# Revit family: Primo S
name_source: partatom
category: Мебель
revit_build: Autodesk Revit 2017 (Build: 20160225_1515(x64)
units: mm (PartAtom-declared; Revit-internal decimal feet)

## family parameters
Всегда вертикально = Да
На основе рабочей плоскости = Нет
Общий = Нет
При загрузке вырезать с полостями = Нет
Точка расчета площади = Нет

## types (6) — shared parameters
Legs Material = Aluminum
Изготовитель = Skandiform AB
Ключевая пометка = XBF.2
Комментарии к типоразмеру = Created by Astacus AB

## per-type parameters (varying)
| type | 092 | 093 | URL | legs type | seat type | Группа модели |
| S-032 | Нет | Нет | http://file-system.ru | Legs 32,33,92&93 | S Seat : S seat | S-032 |
| S-033 | Нет | Нет | http://www.skandiform.com | Legs 32,33,92&93 | H Seat | S-033 |
| S-092 | Да | Нет | http://www.skandiform.com | Legs 32,33,92&93 | S Seat : S seat | S-092 |
| S-082 | Да | Нет | http://www.skandiform.com | Legs 83 | S Seat : S seat | S-092 |
| S-083 | Нет | Нет | http://www.skandiform.com | Legs 83 | H Seat | S-083 |
| S-093 | Нет | Да | http://www.skandiform.com | Legs 32,33,92&93 | H Seat | S-093 |

## geometry (parser evidence)
native form markers: Blend x12, Sweep x19
no freeform markers — native parametric forms only
